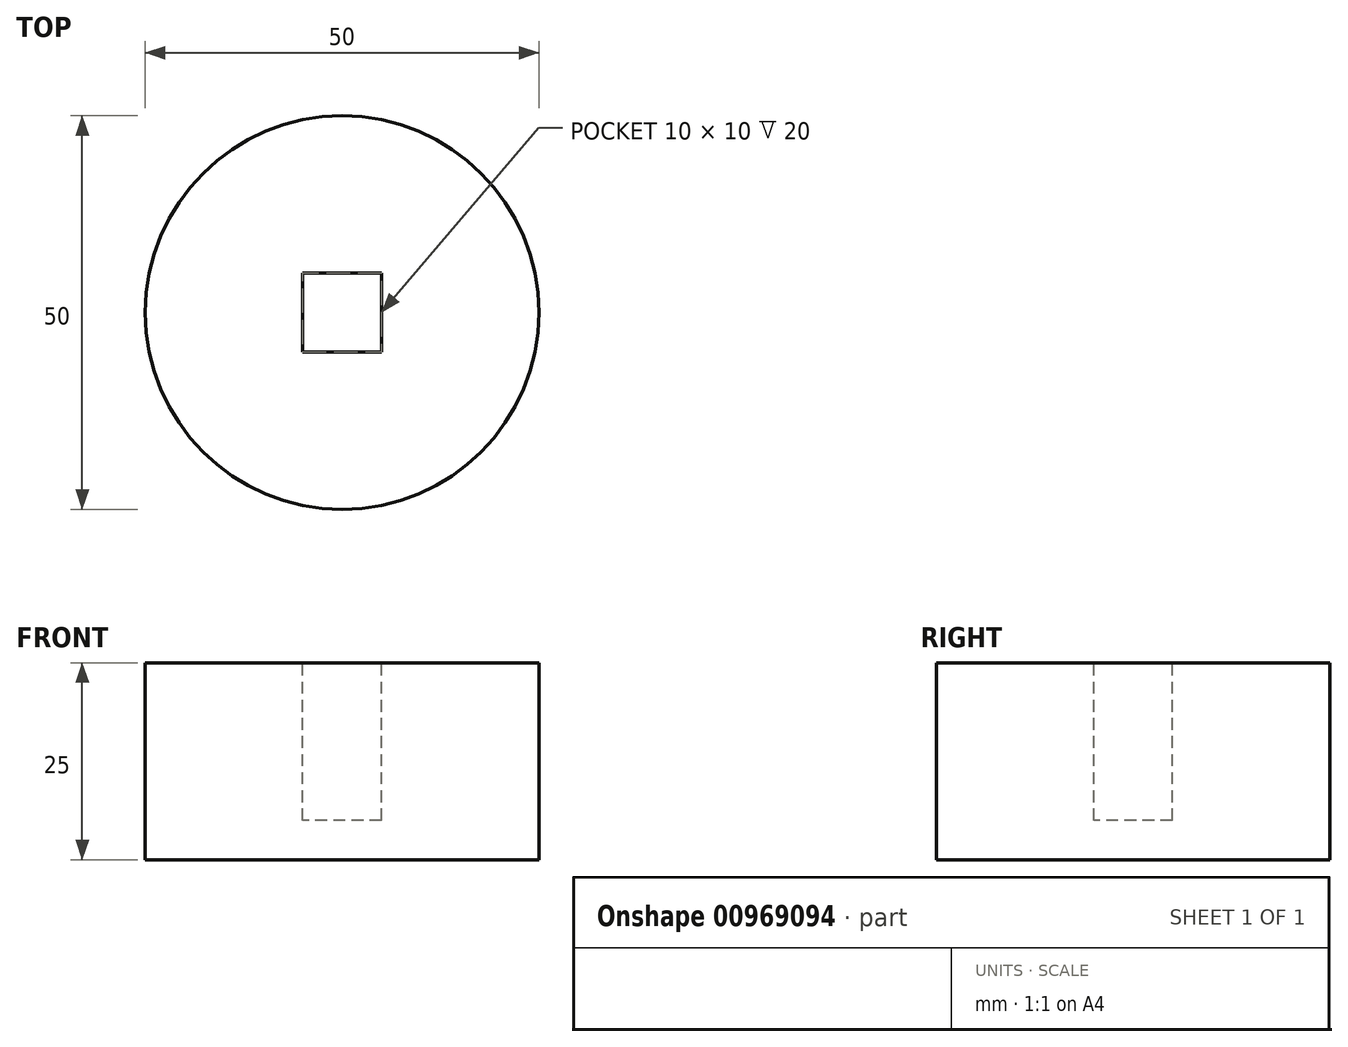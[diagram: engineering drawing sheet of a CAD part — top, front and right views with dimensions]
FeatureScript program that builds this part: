
annotation { "Feature Type Name" : "Feature", "Feature Type Description" : "" }
export const myFeature = defineFeature(function(context is Context, id is Id, definition is map)
    precondition{}
    {
        {
            var Q0;
            Q0=qCreatedBy(makeId("Top.planeOp"),FACE);
            var sketch = newSketch(context, id + "F0", { "sketchPlane" : qUnion([Q0])});
            skCircle(sketch, "E0", {"center": v(0, 0) * mm, "radius": 25 * mm});
            skSolve(sketch);
        }
        {
            var Q0;
            Q0 = qSketchRegion(id + "F0", true);
            extrude(context, id + "F1", {"entities" : qUnion([Q0]), "depth" : 25 * mm, "offsetDistance" : 25 * mm});
        }
        {
            var Q0;
            Q0=makeQuery(id+"F1.opExtrude","CAP_FACE",FACE,{"disambiguationData":[OSD([sQuery(id+"F0.wireOp",EDGE,"E0")])],"isStart":false});
            var sketch = newSketch(context, id + "F2", { "sketchPlane" : qUnion([Q0])});
            skLineSegment(sketch, "E1.bottom", {"start": v(5, 5) * mm, "end": v(-5, 5) * mm});
            skLineSegment(sketch, "E1.top", {"start": v(5, -5) * mm, "end": v(-5, -5) * mm});
            skLineSegment(sketch, "E1.left", {"start": v(5, 5) * mm, "end": v(5, -5) * mm});
            skLineSegment(sketch, "E1.right", {"start": v(-5, 5) * mm, "end": v(-5, -5) * mm});
            skPoint(sketch, "E1.middle", {"position": v(0, 0) * mm});
            skSolve(sketch);
        }
        {
            var Q0;
            Q0=makeQuery(id+"F2.imprint","IMPRINT",FACE,{"disambiguationData":[TD([[makeQuery(id+"F2.imprint","IMPRINT",EDGE,{"derivedFrom":sQuery(id+"F2.wireOp",EDGE,"E1.bottom")}),1.0]])]});
            extrude(context, id + "F3", {"entities" : qUnion([Q0]), "operationType" : NewBodyOperationType.REMOVE, "oppositeDirection" : true, "depth" : 20 * mm, "offsetDistance" : 25 * mm});
        }
    });
